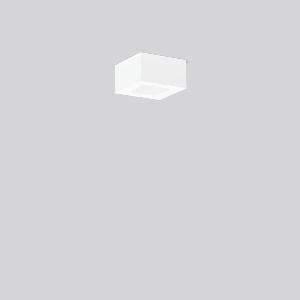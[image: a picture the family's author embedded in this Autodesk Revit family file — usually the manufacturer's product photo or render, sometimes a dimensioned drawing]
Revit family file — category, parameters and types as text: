
# Revit family: toledo_flat_square_a_672259_002_1_1bb3
name_source: partatom
category: Lighting Fixtures
units: mm (PartAtom-declared; Revit-internal decimal feet)

## family parameters
Cut with Voids When Loaded = No
Host = Face
Light Source = No
Part Type = Normal
Room Calculation Point = No
Round Connector Dimension = Use Diameter
Shared = No

## types (1)
- TOLEDO FLAT square A (1 x LED Modul 840, 430 lm, 4000)
    Apparent Load = 6 VA
    CIE Flux Codes = 47 79 96 100 100
    Color Rendering = 80
    Color Temperature = 4000
    Default Elevation = 1800 mm
    Description = Series: TOLEDO FLAT square
Ultra thin surface mounted downlight. For escape route illumination. Surface mounted housing: sheet steel, powder-coated. Square cover plate: die-cast aluminium, powder coated. Light guide and diffuser made of non-yellowing PMMA, opal matt. Driver integrated. Suitable for connection to central battery systems. 
Colour: white
Length: 110 mm
Width: 110 mm
Height: 58 mm
Weight: 560 g
Operating mode: maintained power mode
Lamp: LED
Socket: without socket
Colour temperature: 4000K
Colour rendering index (CRI): 80
System power: 6 W
Rated luminous flux: 430 lm
Luminous flux, emergency: 430 lm
System power, emergency: 6 W
Control gear: Regulated power supply
Protection class: I
Type of protection: IP 40
    Height = 58 mm
    Lamp = 1 x LED Modul 840
    Lamp Light Flux = 430 lm
    Lamp count = 1
    Length = 110 mm
    Lifetime = 50000 h
    Luminous efficacy = 72 lm/W
    Manufacturer = RZB
    ModVariant = No
    Model = 672259.002.1
    Mounting Place = Ceiling
    Mounting Type = Surface mounted
    Number of Poles = 1
    OnlyDefault = Yes
    Power Factor = 1
    Product Name = TOLEDO FLAT square A
    Product group = Surface mounted downlights
    ProductGroupID = 302
    Protection Class = Protection class I
    Protection Degree = IP 40
    RLX_Detail_Level = 1
    RLX_Emergency_Light_Flux = 430 lm
    RLX_Emergency_Type = 3
    RLX_Emergency_Type_DB = Yes
    RlxData = <blob elided: 8589 chars, md5=1b94e963>
    Socket = socket
    Standby Power = 0 W
    System Light Flux = 430 lm
    System Power = 6 W
    Type Comments = Product without accessories
    Type Image = 901551.002.jpg
    URL = http://relux.com
    VarID = ---
    Voltage = 230 V
    Voltage Range = 220-240 V
    Weight = 0.00 kg
    Width = 110 mm

## geometry (parser evidence)
native form markers: Blend x4, Sweep x11
no freeform markers — native parametric forms only
